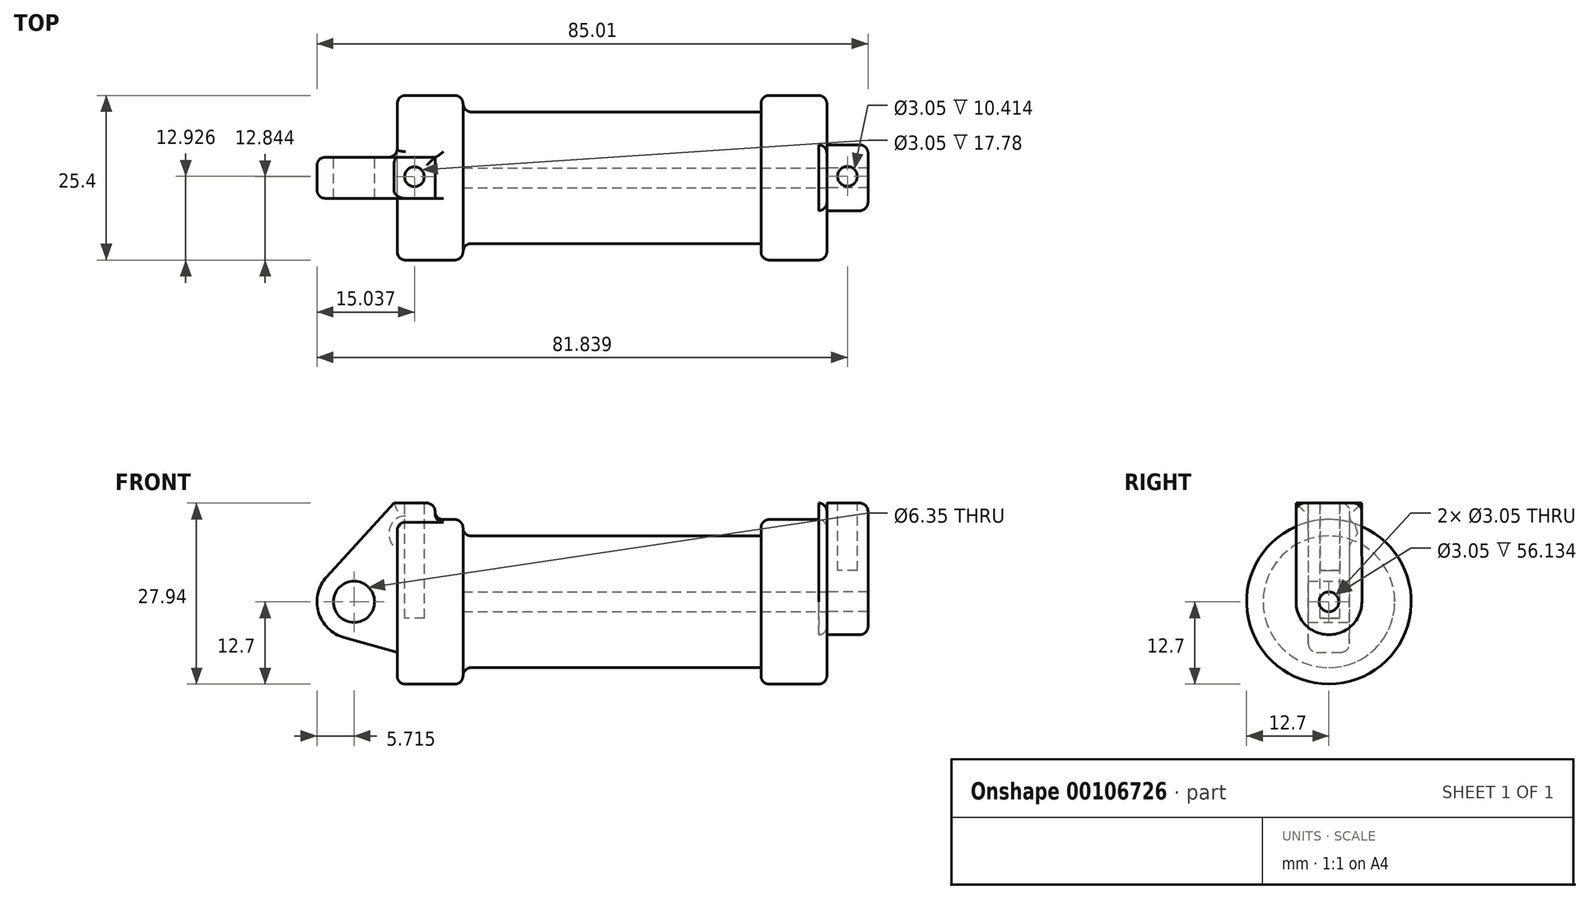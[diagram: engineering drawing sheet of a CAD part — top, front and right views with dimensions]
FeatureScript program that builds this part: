
annotation { "Feature Type Name" : "Feature", "Feature Type Description" : "" }
export const myFeature = defineFeature(function(context is Context, id is Id, definition is map)
    precondition{}
    {
        {
            var Q0;
            Q0=qCreatedBy(makeId("Front.planeOp"),FACE);
            var sketch = newSketch(context, id + "F0", { "sketchPlane" : qUnion([Q0])});
            skLineSegment(sketch, "E0", {"start": v(0, 0) * mm, "end": v(0, 12.7) * mm});
            skLineSegment(sketch, "E1", {"start": v(0, 12.7) * mm, "end": v(10.16, 12.7) * mm});
            skLineSegment(sketch, "E2", {"start": v(10.16, 12.7) * mm, "end": v(10.16, 10.16) * mm});
            skLineSegment(sketch, "E3", {"start": v(10.16, 10.16) * mm, "end": v(56.13, 10.16) * mm});
            skLineSegment(sketch, "E4", {"start": v(56.13, 10.16) * mm, "end": v(56.13, 12.7) * mm});
            skLineSegment(sketch, "E5", {"start": v(56.13, 12.7) * mm, "end": v(66.3, 12.7) * mm});
            skLineSegment(sketch, "E6", {"start": v(66.3, 12.7) * mm, "end": v(66.3, 0) * mm});
            skLineSegment(sketch, "E7", {"start": v(66.3, 0) * mm, "end": v(0, 0) * mm});
            skLineSegment(sketch, "E8", {"start": v(5.84, 15.24) * mm, "end": v(-0.5, 15.24) * mm});
            skLineSegment(sketch, "E9", {"start": v(-0.5, 15.24) * mm, "end": v(-10.88, 3.85) * mm});
            skLineSegment(sketch, "E10", {"start": v(0, 0) * mm, "end": v(-6.65, 0) * mm});
            skCircle(sketch, "E11", {"center": v(-6.65, 0) * mm, "radius": 5.72 * mm});
            skCircle(sketch, "E12", {"center": v(-6.65, 0) * mm, "radius": 3.18 * mm});
            skLineSegment(sketch, "E13", {"start": v(5.84, 15.24) * mm, "end": v(5.84, -9.4) * mm});
            skLineSegment(sketch, "E14", {"start": v(5.84, -9.4) * mm, "end": v(-8.18, -5.5) * mm});
            skSolve(sketch);
        }
        {
            var Q0;
            {var subQ0=sQuery(id+"F0.wireOp",EDGE,"E0");Q0=makeQuery(id+"F0.imprint","IMPRINT",FACE,{"disambiguationData":[TD([[makeQuery(id+"F0.imprint","IMPRINT",EDGE,{"derivedFrom":subQ0}),-1.0]])]});}
            var Q1;
            {var subQ0=sQuery(id+"F0.wireOp",EDGE,"E2");Q1=makeQuery(id+"F0.imprint","IMPRINT",FACE,{"disambiguationData":[TD([[makeQuery(id+"F0.imprint","IMPRINT",EDGE,{"derivedFrom":subQ0}),-1.0]])]});}
            var Q2;
            Q2=sQuery(id+"F0.wireOp",EDGE,"E7");
            revolve(context, id + "F1", {"entities" : qUnion([Q0, Q1]), "axis" : qUnion([Q2]), "revolveType" : RevolveType.FULL});
        }
        {
            var Q0;
            {var subQ0=sQuery(id+"F0.wireOp",EDGE,"E14");Q0=makeQuery(id+"F0.imprint","IMPRINT",FACE,{"disambiguationData":[TD([[makeQuery(id+"F0.imprint","IMPRINT",EDGE,{"derivedFrom":subQ0}),-1.0]])]});}
            var Q1;
            {var subQ4=sQuery(id+"F0.wireOp",EDGE,"E12");Q1=makeQuery(id+"F0.imprint","IMPRINT",FACE,{"disambiguationData":[TD([[makeQuery(id+"F0.imprint","IMPRINT",EDGE,{"derivedFrom":subQ4}),-1.0]])]});}
            var Q2;
            {var subQ3=sQuery(id+"F0.wireOp",EDGE,"E0");Q2=makeQuery(id+"F0.imprint","IMPRINT",FACE,{"disambiguationData":[TD([[makeQuery(id+"F0.imprint","IMPRINT",EDGE,{"derivedFrom":subQ3}),1.0]])]});}
            var Q3;
            {var subQ0=sQuery(id+"F0.wireOp",EDGE,"E0");Q3=makeQuery(id+"F0.imprint","IMPRINT",FACE,{"disambiguationData":[TD([[makeQuery(id+"F0.imprint","IMPRINT",EDGE,{"derivedFrom":subQ0}),-1.0]])]});}
            extrude(context, id + "F2", {"entities" : qUnion([Q0, Q1, Q2, Q3]), "operationType" : NewBodyOperationType.ADD, "endBound" : BoundingType.SYMMETRIC, "depth" : 6.35 * mm});
        }
        {
            var Q0;
            Q0=makeQuery(id+"F1.opRevolve","SWEPT_FACE",FACE,{"disambiguationData":[OSD([sQuery(id+"F0.wireOp",EDGE,"E6")])]});
            var sketch = newSketch(context, id + "F3", { "sketchPlane" : qUnion([Q0])});
            skCircle(sketch, "E15", {"center": v(0, 0) * mm, "radius": 5.08 * mm});
            skCircle(sketch, "E16", {"center": v(0, 0) * mm, "radius": 1.52 * mm});
            skLineSegment(sketch, "E17", {"start": v(-5.08, 0) * mm, "end": v(-5.08, 14.91) * mm});
            skLineSegment(sketch, "E18", {"start": v(5.08, 0) * mm, "end": v(5.07, 15.24) * mm});
            skLineSegment(sketch, "E19", {"start": v(5.07, 15.24) * mm, "end": v(-5.08, 15.24) * mm});
            skLineSegment(sketch, "E20", {"start": v(-5.08, 15.24) * mm, "end": v(-5.08, 14.91) * mm});
            skSolve(sketch);
        }
        {
            var Q0;
            {var subQ0=sQuery(id+"F3.wireOp",EDGE,"E17");var subQ1=sQuery(id+"F3.wireOp",EDGE,"E15");var subQ2=makeQuery(id+"F3.imprint","INTERSECT",VERTEX,{"derivedFrom":[subQ1,subQ0]});Q0=makeQuery(id+"F3.imprint","IMPRINT",FACE,{"disambiguationData":[TD([[makeQuery(id+"F3.imprint","IMPRINT",EDGE,{"disambiguationData":[TD([[subQ2,1.0]])],"derivedFrom":subQ1}),-1.0]])]});}
            var Q1;
            {var subQ0=sQuery(id+"F3.wireOp",EDGE,"E19");Q1=makeQuery(id+"F3.imprint","IMPRINT",FACE,{"disambiguationData":[TD([[makeQuery(id+"F3.imprint","IMPRINT",EDGE,{"derivedFrom":subQ0}),1.0]])]});}
            var Q2;
            Q2=makeQuery(id+"F3.imprint","IMPRINT",FACE,{"disambiguationData":[TD([[makeQuery(id+"F3.imprint","IMPRINT",EDGE,{"derivedFrom":sQuery(id+"F3.wireOp",EDGE,"E16")}),-1.0]])]});
            extrude(context, id + "F4", {"entities" : qUnion([Q0, Q1, Q2]), "oppositeDirection" : true, "depth" : 1.27 * mm});
        }
        {
            var Q0;
            Q0=makeQuery(id+"F4.opExtrude","CAP_FACE",FACE,{"disambiguationData":[OSD([sQuery(id+"F3.wireOp",EDGE,"E15"),sQuery(id+"F3.wireOp",EDGE,"E16"),sQuery(id+"F3.wireOp",EDGE,"E17"),sQuery(id+"F3.wireOp",EDGE,"E18"),sQuery(id+"F3.wireOp",EDGE,"E19"),sQuery(id+"F3.wireOp",EDGE,"E20")])],"isStart":true});
            extrude(context, id + "F5", {"entities" : qUnion([Q0]), "depth" : 6.35 * mm});
        }
        {
            var Q0;
            Q0=makeQuery(id+"F3.imprint","IMPRINT",FACE,{"disambiguationData":[TD([[makeQuery(id+"F3.imprint","IMPRINT",EDGE,{"derivedFrom":sQuery(id+"F3.wireOp",EDGE,"E16")}),1.0]])]});
            var Q1;
            Q1=makeQuery(id+"F1.opRevolve","SWEPT_FACE",FACE,{"disambiguationData":[OSD([sQuery(id+"F0.wireOp",EDGE,"E2")])]});
            extrude(context, id + "F6", {"entities" : qUnion([Q0]), "operationType" : NewBodyOperationType.REMOVE, "endBound" : BoundingType.UP_TO_SURFACE, "oppositeDirection" : true, "endBoundEntityFace" : qUnion([Q1]), "depth" : 25.4 * mm});
        }
        {
            var Q0;
            Q0=makeQuery(id+"F2.opExtrude","SWEPT_FACE",FACE,{"disambiguationData":[OSD([sQuery(id+"F0.wireOp",EDGE,"E8")])]});
            var sketch = newSketch(context, id + "F7", { "sketchPlane" : qUnion([Q0])});
            skCircle(sketch, "E21", {"center": v(2.67, 0.14) * mm, "radius": 1.52 * mm});
            skPoint(sketch, "E21.centerSnap0", {"position": v(2.67, -3.18) * mm});
            skSolve(sketch);
        }
        {
            var Q0;
            Q0=makeQuery(id+"F5.opExtrude","SWEPT_FACE",FACE,{"disambiguationData":[OSD([sQuery(id+"F3.wireOp",EDGE,"E19")])]});
            var sketch = newSketch(context, id + "F8", { "sketchPlane" : qUnion([Q0])});
            skCircle(sketch, "E22", {"center": v(69.47, 0.23) * mm, "radius": 1.52 * mm});
            skPoint(sketch, "E22.centerSnap0", {"position": v(69.47, -5.08) * mm});
            skSolve(sketch);
        }
        {
            var Q0;
            Q0=makeQuery(id+"F7.imprint","IMPRINT",FACE,{"disambiguationData":[TD([[makeQuery(id+"F7.imprint","IMPRINT",EDGE,{"derivedFrom":sQuery(id+"F7.wireOp",EDGE,"E21")}),1.0]])]});
            extrude(context, id + "F9", {"entities" : qUnion([Q0]), "operationType" : NewBodyOperationType.REMOVE, "oppositeDirection" : true, "depth" : 17.78 * mm});
        }
        {
            var Q0;
            Q0=makeQuery(id+"F8.imprint","IMPRINT",FACE,{"disambiguationData":[TD([[makeQuery(id+"F8.imprint","IMPRINT",EDGE,{"derivedFrom":sQuery(id+"F8.wireOp",EDGE,"E22")}),1.0]])]});
            extrude(context, id + "F10", {"entities" : qUnion([Q0]), "operationType" : NewBodyOperationType.REMOVE, "oppositeDirection" : true, "depth" : 10.4 * mm});
        }
        {
            var Q0;
            Q0=makeQuery(id+"F2.opExtrude","CAP_EDGE",EDGE,{"disambiguationData":[OSD([sQuery(id+"F0.wireOp",EDGE,"E9")])],"isStart":true});
            var Q1;
            Q1=makeQuery(id+"F2.opExtrude","CAP_EDGE",EDGE,{"disambiguationData":[OSD([sQuery(id+"F0.wireOp",EDGE,"E8")])],"isStart":true});
            var Q2;
            Q2=makeQuery(id+"F1.opRevolve","SWEPT_EDGE",EDGE,{"disambiguationData":[OSD([sQuery(id+"F0.wireOp",EDGE,"E1"),sQuery(id+"F0.wireOp",EDGE,"E2")])]});
            var Q3;
            Q3=makeQuery(id+"F1.opRevolve","SWEPT_EDGE",EDGE,{"disambiguationData":[OSD([sQuery(id+"F0.wireOp",EDGE,"E2"),sQuery(id+"F0.wireOp",EDGE,"E3")])]});
            var Q4;
            Q4=makeQuery(id+"F2.opExtrude","SWEPT_EDGE",EDGE,{"disambiguationData":[OSD([sQuery(id+"F0.wireOp",EDGE,"E8"),sQuery(id+"F0.wireOp",EDGE,"E13")])]});
            var Q5;
            Q5=makeQuery(id+"F2.boolean.opBoolean","INTERSECT",EDGE,{"derivedFrom":[makeQuery(id+"F1.opRevolve","SWEPT_FACE",FACE,{"disambiguationData":[OSD([sQuery(id+"F0.wireOp",EDGE,"E1")])]}),makeQuery(id+"F2.opExtrude","SWEPT_FACE",FACE,{"disambiguationData":[OSD([sQuery(id+"F0.wireOp",EDGE,"E13")])]})]});
            var Q6;
            Q6=makeQuery(id+"F2.boolean.opBoolean","INTERSECT",EDGE,{"derivedFrom":[makeQuery(id+"F1.opRevolve","SWEPT_FACE",FACE,{"disambiguationData":[OSD([sQuery(id+"F0.wireOp",EDGE,"E1")])]}),makeQuery(id+"F2.opExtrude","CAP_FACE",FACE,{"disambiguationData":[OSD([sQuery(id+"F0.wireOp",EDGE,"E8"),sQuery(id+"F0.wireOp",EDGE,"E9"),sQuery(id+"F0.wireOp",EDGE,"E11"),sQuery(id+"F0.wireOp",EDGE,"E12"),sQuery(id+"F0.wireOp",EDGE,"E13"),sQuery(id+"F0.wireOp",EDGE,"E14")])],"isStart":true})]});
            var Q7;
            Q7=makeQuery(id+"F1.opRevolve","SWEPT_EDGE",EDGE,{"disambiguationData":[OSD([sQuery(id+"F0.wireOp",EDGE,"E0"),sQuery(id+"F0.wireOp",EDGE,"E1")])]});
            var Q8;
            Q8=makeQuery(id+"F2.opExtrude","CAP_EDGE",EDGE,{"disambiguationData":[OSD([sQuery(id+"F0.wireOp",EDGE,"E14")])],"isStart":false});
            var Q9;
            Q9=makeQuery(id+"F1.opRevolve","SWEPT_EDGE",EDGE,{"disambiguationData":[OSD([sQuery(id+"F0.wireOp",EDGE,"E4"),sQuery(id+"F0.wireOp",EDGE,"E5")])]});
            var Q10;
            Q10=makeQuery(id+"F1.opRevolve","SWEPT_EDGE",EDGE,{"disambiguationData":[OSD([sQuery(id+"F0.wireOp",EDGE,"E5"),sQuery(id+"F0.wireOp",EDGE,"E6")])]});
            var Q11;
            Q11=makeQuery(id+"F4.opExtrude","CAP_EDGE",EDGE,{"disambiguationData":[OSD([sQuery(id+"F3.wireOp",EDGE,"E17"),sQuery(id+"F3.wireOp",EDGE,"E20")])],"isStart":true});
            var Q12;
            Q12=makeQuery(id+"F5.opExtrude","CAP_EDGE",EDGE,{"disambiguationData":[OSD([sQuery(id+"F3.wireOp",EDGE,"E17"),sQuery(id+"F3.wireOp",EDGE,"E20")])],"isStart":false});
            var Q13;
            Q13=makeQuery(id+"F5.opExtrude","SWEPT_EDGE",EDGE,{"disambiguationData":[OSD([sQuery(id+"F3.wireOp",EDGE,"E19"),sQuery(id+"F3.wireOp",EDGE,"E20")])]});
            var Q14;
            Q14=makeQuery(id+"F5.opExtrude","SWEPT_EDGE",EDGE,{"disambiguationData":[OSD([sQuery(id+"F3.wireOp",EDGE,"E18"),sQuery(id+"F3.wireOp",EDGE,"E19")])]});
            var Q15;
            Q15=makeQuery(id+"F5.opExtrude","CAP_EDGE",EDGE,{"disambiguationData":[OSD([sQuery(id+"F3.wireOp",EDGE,"E19")])],"isStart":false});
            var Q16;
            Q16=makeQuery(id+"F4.opExtrude","CAP_EDGE",EDGE,{"disambiguationData":[OSD([sQuery(id+"F3.wireOp",EDGE,"E19")])],"isStart":true});
            fillet(context, id + "F11", {"entities" : qUnion([Q0, Q1, Q2, Q3, Q4, Q5, Q6, Q7, Q8, Q9, Q10, Q11, Q12, Q13, Q14, Q15, Q16]), "radius" : 1.27 * mm, "tangentPropagation" : true, "allowEdgeOverflow" : false});
        }
    });
